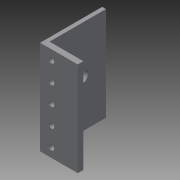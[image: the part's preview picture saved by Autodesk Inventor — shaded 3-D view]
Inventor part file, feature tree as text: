
AUTODESK INVENTOR PART (.ipt)
format: ipt  version: 2013 (Build 170138000, 138)  size: 100,864 bytes
history: native  units: mm
features: sketch x4, extrude x2, hole x2, other x1
ambient origin geometry x8: Origin, YZ Plane, XZ Plane, XY Plane, X Axis, Y Axis, Z Axis, Center Point
feature tree (9):
  other  "ソリッド1"
  extrude  "押し出し1"  Depth=20.0mm
  extrude  "押し出し2"  Depth=50.0mm
  hole  "穴1"  [1 undecoded]
  hole  "穴2"  [1 undecoded]
  sketch  "スケッチ1"
  sketch  "スケッチ2"
  sketch  "スケッチ3"
  sketch  "スケッチ4"
note: 2 required parameter values undecoded (feature->parameter linkage not recoverable at this tier; creation-order binding heuristic only, values carry confidence <= 0.55)
